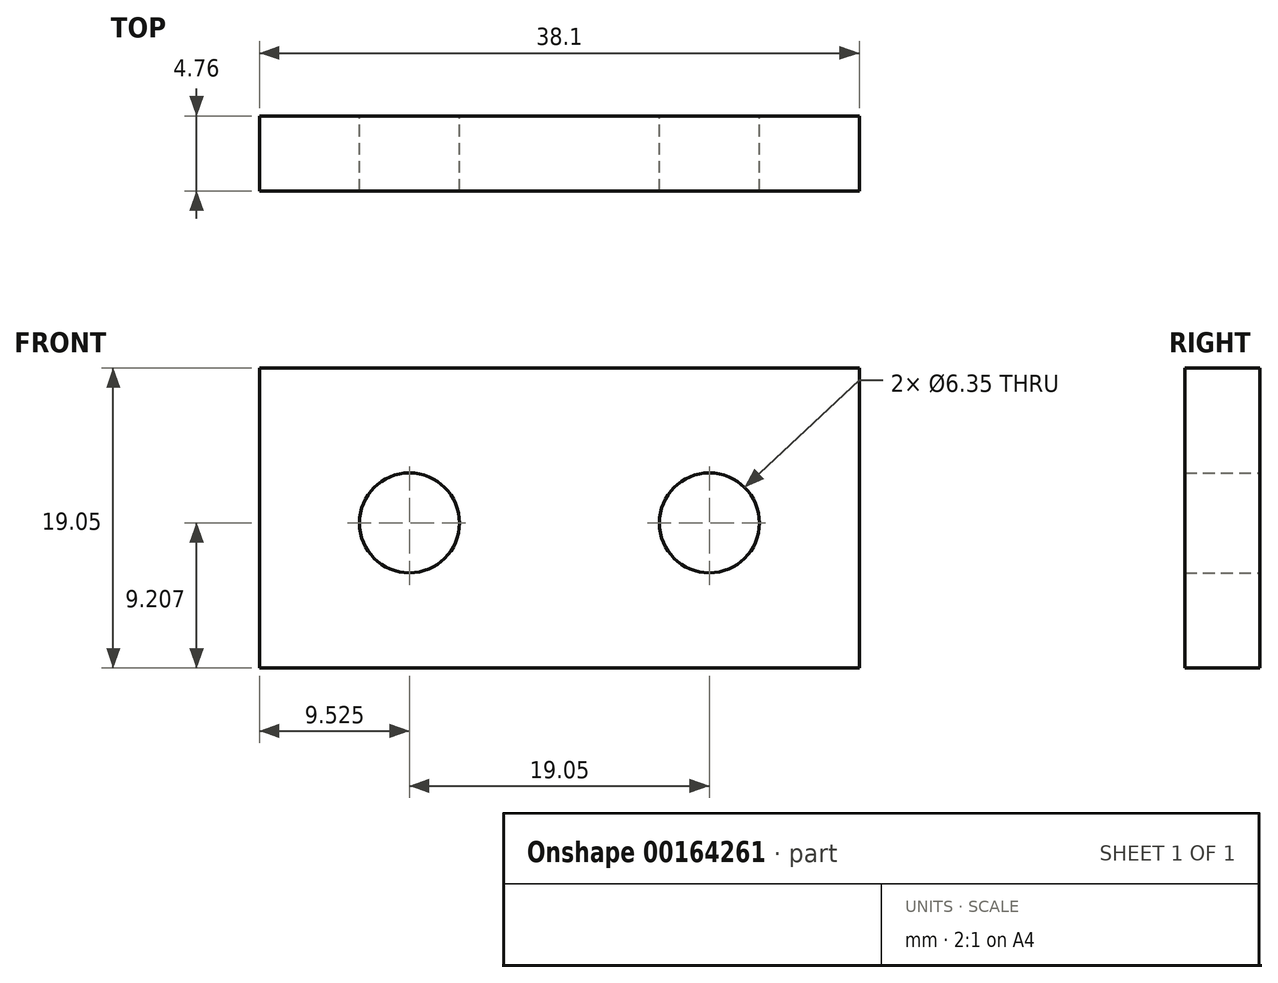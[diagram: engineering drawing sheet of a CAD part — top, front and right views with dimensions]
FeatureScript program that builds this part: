
annotation { "Feature Type Name" : "Feature", "Feature Type Description" : "" }
export const myFeature = defineFeature(function(context is Context, id is Id, definition is map)
    precondition{}
    {
        {
            var Q0;
            Q0=qCreatedBy(makeId("Front.planeOp"),FACE);
            var sketch = newSketch(context, id + "F0", { "sketchPlane" : qUnion([Q0])});
            skLineSegment(sketch, "E0", {"start": v(0, 0) * mm, "end": v(38.1, 0) * mm});
            skLineSegment(sketch, "E1", {"start": v(38.1, 0) * mm, "end": v(38.1, 19.05) * mm});
            skLineSegment(sketch, "E2", {"start": v(38.1, 19.05) * mm, "end": v(0, 19.05) * mm});
            skLineSegment(sketch, "E3", {"start": v(0, 19.05) * mm, "end": v(0, 0) * mm});
            skCircle(sketch, "E4", {"center": v(28.58, 9.2) * mm, "radius": 3.18 * mm});
            skCircle(sketch, "E5", {"center": v(9.53, 9.2) * mm, "radius": 3.18 * mm});
            skLineSegment(sketch, "E6", {"start": v(9.53, 9.2) * mm, "end": v(28.58, 9.2) * mm, "construction": true});
            skLineSegment(sketch, "E7", {"start": v(19.05, 9.2) * mm, "end": v(19.05, 0) * mm, "construction": true});
            skPoint(sketch, "E7.endSnap0", {"position": v(19.05, 9.2) * mm});
            skSolve(sketch);
        }
        {
            var Q0;
            Q0=makeQuery(id+"F0.imprint","IMPRINT",FACE,{"disambiguationData":[TD([[makeQuery(id+"F0.imprint","IMPRINT",EDGE,{"derivedFrom":sQuery(id+"F0.wireOp",EDGE,"E0")}),1.0]])]});
            extrude(context, id + "F1", {"entities" : qUnion([Q0]), "depth" : 4.76 * mm});
        }
    });
